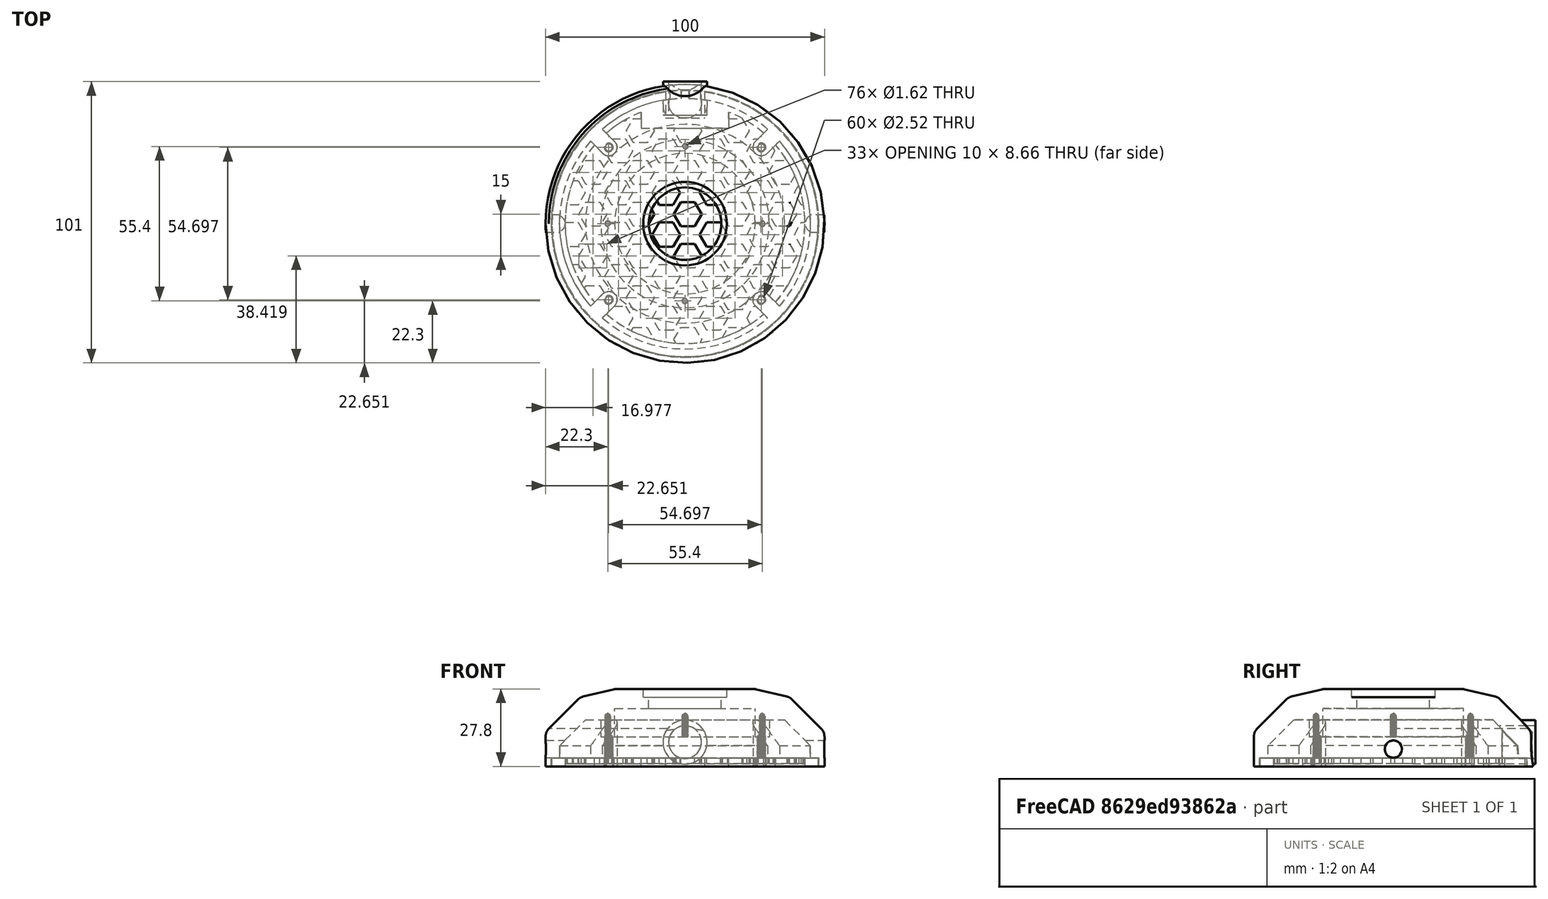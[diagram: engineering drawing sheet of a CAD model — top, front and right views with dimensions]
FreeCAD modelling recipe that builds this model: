
FCSTD DOCUMENT  (FreeCAD 0.22R37898 (Git))
Label: headset cup
License: All rights reserved
objects: Sketcher::SketchObject×12, PartDesign::Pad×4, PartDesign::Pocket×4, PartDesign::Body×3, PartDesign::PolarPattern×2, PartDesign::Hole×2, PartDesign::LinearPattern×2, PartDesign::Revolution×1, PartDesign::ShapeBinder×1, PartDesign::MultiTransform×1, PartDesign::Boolean×1, PartDesign::Fillet×1
note: 46 computed .brp shape members not serialized (recipe doc carries the construction recipe); baked Part::Feature solids carry a one-line shape summary decoded from their .brp

FEATURE [Sketcher::SketchObject] Sketch
  AttachmentSupport = -> [XZ_Plane]
  FullyConstrained = false
  MapMode = 5
  Placement = pos=(0,0,0) rot=(1,0,0;1.5708rad)
  sketch-geometry (23):
    g0: LineSegment StartX=-50 StartY=0 StartZ=0 EndX=-50 EndY=12.4 EndZ=0
    g1: LineSegment StartX=-50 StartY=12.4 StartZ=0 EndX=-37.6 EndY=12.4 EndZ=0
    g2: LineSegment StartX=-37.6 StartY=12.4 StartZ=0 EndX=-37.6 EndY=24.8 EndZ=0
    g3: LineSegment StartX=-50 StartY=12.4 StartZ=0 EndX=-37.6 EndY=24.8 EndZ=0
    g4: LineSegment StartX=-37.6 StartY=24.8 StartZ=0 EndX=0 EndY=24.8 EndZ=0
    g5: LineSegment StartX=-25 StartY=27.8 StartZ=0 EndX=-25 EndY=0.000476786 EndZ=0
    g6: LineSegment StartX=-37.6 StartY=24.8 StartZ=0 EndX=-25 EndY=27.8 EndZ=0
    g7: LineSegment StartX=-50 StartY=0 StartZ=0 EndX=-48 EndY=0 EndZ=0
    g8: LineSegment StartX=-48 StartY=0 StartZ=0 EndX=-48 EndY=3 EndZ=0
    g9: LineSegment StartX=-48 StartY=3 StartZ=0 EndX=-45 EndY=3 EndZ=0
    g10: LineSegment StartX=-45 StartY=7.4 StartZ=0 EndX=-45 EndY=3 EndZ=0
    g11: LineSegment StartX=-50 StartY=12.4 StartZ=0 EndX=-45 EndY=7.4 EndZ=0
    g12: LineSegment StartX=-45 StartY=7.4 StartZ=0 EndX=-35.6769 EndY=16.7231 EndZ=0
    g13: LineSegment StartX=-37.6 StartY=24.8 StartZ=0 EndX=-35.6769 EndY=16.7231 EndZ=0
    g14: LineSegment StartX=-30.2 StartY=10.6 StartZ=0 EndX=-25.2 EndY=10.6 EndZ=0
    g15: LineSegment StartX=-35.6769 StartY=16.7231 StartZ=0 EndX=-30.2 EndY=16.7231 EndZ=0
    g16: LineSegment StartX=-30.2 StartY=16.7231 StartZ=0 EndX=-30.2 EndY=10.6 EndZ=0
    g17: LineSegment StartX=-25.2 StartY=10.6 StartZ=0 EndX=-25.2 EndY=20.8 EndZ=0
    g18: LineSegment StartX=-25.2 StartY=20.8 StartZ=0 EndX=-13 EndY=20.8 EndZ=0
    g19: LineSegment StartX=-15 StartY=27.8 StartZ=0 EndX=-25 EndY=27.8 EndZ=0
    g20: LineSegment StartX=-13 StartY=20.8 StartZ=0 EndX=-13 EndY=24.8 EndZ=0
    g21: LineSegment StartX=-13 StartY=24.8 StartZ=0 EndX=-15 EndY=24.8 EndZ=0
    g22: LineSegment StartX=-15 StartY=24.8 StartZ=0 EndX=-15 EndY=27.8 EndZ=0
  constraints (63):
    c: PointOnObject(g0,g-1)
    c: Distance(g0) = 12.4
    c: Vertical(g0)
    c: Distance(g1) = 12.4
    c: Coincident(g1,g0)
    c: Horizontal(g1)
    c: Distance(g2) = 12.4
    c: Coincident(g2,g1)
    c: Vertical(g2)
    c: Coincident(g3,g0)
    c: Coincident(g3,g2)
    c: Coincident(g4,g2)
    c: PointOnObject(g4,g-2)
    c: Horizontal(g4)
    c: Vertical(g5)
    c: Distance(g-2,g5) = 25
    c: Coincident(g6,g2)
    c: Block(g6)
    c: Distance(g7) = 2
    c: Coincident(g7,g0)
    c: PointOnObject(g7,g-1)
    c: Distance(g8) = 3
    c: Coincident(g8,g7)
    c: Vertical(g8)
    c: Distance(g9) = 3
    c: Coincident(g9,g8)
    c: Horizontal(g9)
    c: Vertical(g10)
    c: Coincident(g10,g9)
    c: Coincident(g11,g0)
    c: Angle(g11,g3) = 1.5708
    c: Coincident(g11,g10)
    c: Coincident(g12,g10)
    c: Parallel(g12,g3)
    c: Coincident(g13,g2)
    c: Perpendicular(g6,g13)
    c: Coincident(g12,g13)
    c: Horizontal(g14)
    c: Coincident(g15,g12)
    c: Horizontal(g15)
    c: Distance(g15,g5) = 5.2
    c: Coincident(g16,g15)
    c: Vertical(g16)
    c: Coincident(g14,g16)
    c: Distance(g6,g14) = 17.2
    c: Coincident(g5,g6)
    c: Coincident(g17,g14)
    c: Vertical(g17)
    c: Distance(g17,g4) = 4
    c: Perpendicular(g18,g17) = 1.5708
    c: Coincident(g19,g5)
    c: Horizontal(g19)
    c: Distance(g5,g17) = 0.2
    c: Distance(g18,g18) = 12.2
    c: Coincident(g20,g18)
    c: PointOnObject(g20,g4)
    c: Vertical(g20)
    c: Coincident(g21,g20)
    c: PointOnObject(g21,g4)
    c: Coincident(g22,g21)
    c: Vertical(g22)
    c: Coincident(g22,g19)
    c: DistanceX(g21,g21) = 2
FEATURE [Sketcher::SketchObject] Sketch003
  FullyConstrained = false
  MapMode = 5
  Placement = pos=(0,7e-16,3) rot=(1,0,0;3.14159rad)
  sketch-geometry (4):
    g0: Circle CenterX=-0.037202 CenterY=-40.3385 CenterZ=0 NormalX=0 NormalY=0 NormalZ=1 AngleXU=0 Radius=1.53995
    g1: Circle CenterX=40.3385 CenterY=-0.037202 CenterZ=0 NormalX=0 NormalY=0 NormalZ=1 AngleXU=0 Radius=1.48786
    g2: Circle CenterX=0.037202 CenterY=40.3385 CenterZ=0 NormalX=0 NormalY=0 NormalZ=1 AngleXU=0 Radius=1.46013
    g3: Circle CenterX=-40.3385 CenterY=0.037202 CenterZ=0 NormalX=0 NormalY=0 NormalZ=1 AngleXU=0 Radius=1.54339
FEATURE [PartDesign::Revolution] Revolution
  Angle = 360
  Angle2 = 60
  Axis = (0,2e-16,1)
  Base = (0,0,0)
  Placement = pos=(0,0,0) rot=(1,0,0;1.5708rad)
  Profile = -> Sketch
  ReferenceAxis = -> Sketch [V_Axis]
  Refine = true
  Suppressed = false
  Type = 0
FEATURE [Sketcher::SketchObject] Sketch004  label="support for screws"
  AttachmentSupport = -> [Revolution]
  FullyConstrained = false
  MapMode = 5
  Placement = pos=(0,7e-16,3) rot=(1,0,0;3.14159rad)
  sketch-geometry (6):
    g0: LineSegment StartX=0 StartY=0 StartZ=0 EndX=54.6974 EndY=54.6974 EndZ=0
    g1: Circle CenterX=27.3487 CenterY=27.3487 CenterZ=0 NormalX=0 NormalY=0 NormalZ=1 AngleXU=0 Radius=1.5
    g2: ArcOfCircle CenterX=27.3487 CenterY=27.3487 CenterZ=0 NormalX=0 NormalY=0 NormalZ=1 AngleXU=0 Radius=3 StartAngle=2.3562 EndAngle=5.49778
    g3: ArcOfCircle CenterX=9.84391e-06 CenterY=0 CenterZ=0 NormalX=0 NormalY=0 NormalZ=1 AngleXU=0 Radius=45 StartAngle=0.718682 EndAngle=0.852114
    g4: LineSegment StartX=25.2274 StartY=29.47 StartZ=0 EndX=29.6277 EndY=33.8703 EndZ=0
    g5: LineSegment StartX=33.8703 StartY=29.6277 StartZ=0 EndX=29.47 EndY=25.2274 EndZ=0
  constraints (14):
    c: Coincident(g0,g-1)
    c: Diameter(g1) = 3
    c: Symmetric(g0,g0,g1)
    c: Tangent(g2,g1) = -1.5708
    c: Coincident(g4,g2)
    c: Coincident(g4,g3)
    c: Coincident(g5,g3)
    c: Coincident(g5,g2)
    c: Equal(g5,g4)
    c: Parallel(g5,g0)
    c: Parallel(g4,g0)
    c: Block(g3)
    c: Radius(g2) = 3
    c: Angle(g0,g-2) = 0.785398
FEATURE [PartDesign::Pad] Pad  label="support screws"
  BaseFeature = -> Revolution
  Direction = (0,0,-1)
  Length = 10
  Length2 = 10
  Placement = pos=(0,0,0) rot=(1,0,0;1.5708rad)
  Profile = -> Sketch004
  ReferenceAxis = -> Sketch004 [N_Axis]
  Refine = true
  Reversed = true
  Suppressed = false
  Type = 5
FEATURE [Sketcher::SketchObject] Sketch005
  FullyConstrained = false
  MapMode = 5
  Placement = pos=(0,7e-16,3) rot=(1,0,0;3.14159rad)
  sketch-geometry (4):
    g0: Circle CenterX=-27.3487 CenterY=27.3487 CenterZ=0 NormalX=0 NormalY=0 NormalZ=1 AngleXU=0 Radius=1.5
    g1: Circle CenterX=27.3487 CenterY=27.3487 CenterZ=0 NormalX=0 NormalY=0 NormalZ=1 AngleXU=0 Radius=1.5
    g2: Circle CenterX=27.3487 CenterY=-27.3487 CenterZ=0 NormalX=0 NormalY=0 NormalZ=1 AngleXU=0 Radius=1.5
    g3: Circle CenterX=-27.3487 CenterY=-27.3487 CenterZ=0 NormalX=0 NormalY=0 NormalZ=1 AngleXU=0 Radius=1.5
  constraints (4):
    c: Diameter(g0) = 3
    c: Diameter(g1) = 3
    c: Diameter(g2) = 3
    c: Diameter(g3) = 3
FEATURE [Sketcher::SketchObject] Sketch006
  FullyConstrained = false
  MapMode = 5
  Placement = pos=(58,0,0) rot=(0.57735,0.57735,0.57735;2.0944rad)
  sketch-geometry (3):
    g0: LineSegment StartX=2.9e-15 StartY=12.4 StartZ=0 EndX=0 EndY=0 EndZ=0
    g1: LineSegment StartX=-10.7592 StartY=6.2 StartZ=0 EndX=0 EndY=6.2 EndZ=0
    g2: Circle CenterX=0 CenterY=6.2 CenterZ=0 NormalX=0 NormalY=0 NormalZ=1 AngleXU=0 Radius=3.1
  constraints (5):
    c: Coincident(g0,g-1)
    c: Symmetric(g0,g0,g1)
    c: PointOnObject(g1,g0)
    c: Diameter(g2) = 6.2
    c: Coincident(g2,g1)
FEATURE [Sketcher::SketchObject] Sketch007
  FullyConstrained = false
  MapMode = 5
  Placement = pos=(0,2.4e-15,10.6) rot=(1,0,0;3.14159rad)
  sketch-geometry (5):
    g0: LineSegment StartX=-7.92396 StartY=-25.2 StartZ=0 EndX=7.02985 EndY=-25.2 EndZ=0
    g1: LineSegment StartX=-7.20371 StartY=-30.2 StartZ=0 EndX=7.21561 EndY=-30.2 EndZ=0
    g2: LineSegment StartX=0 StartY=-25.2 StartZ=0 EndX=0 EndY=-30.2 EndZ=0
    g3: LineSegment StartX=-3.01823 StartY=-27.7 StartZ=0 EndX=0 EndY=-27.7 EndZ=0
    g4: Circle CenterX=0 CenterY=-27.7 CenterZ=0 NormalX=0 NormalY=0 NormalZ=1 AngleXU=0 Radius=1
  constraints (9):
    c: Horizontal(g0)
    c: Horizontal(g1)
    c: PointOnObject(g2,g0)
    c: PointOnObject(g2,g1)
    c: Horizontal(g3)
    c: Symmetric(g2,g2,g3)
    c: PointOnObject(g3,g2)
    c: Diameter(g4) = 2
    c: Coincident(g4,g3)
FEATURE [Sketcher::SketchObject] Sketch008
  FullyConstrained = false
  MapMode = 5
  Placement = pos=(0,38,4) rot=(1,0,0;1.5708rad)
  sketch-geometry (3):
    g0: LineSegment StartX=-2.7e-15 StartY=9.4 StartZ=0 EndX=0 EndY=0 EndZ=0
    g1: LineSegment StartX=-8.38522 StartY=4.7 StartZ=0 EndX=-1.8e-15 EndY=4.7 EndZ=0
    g2: Circle CenterX=-1.8e-15 CenterY=4.7 CenterZ=0 NormalX=0 NormalY=0 NormalZ=1 AngleXU=0 Radius=5.85
  constraints (5):
    c: Coincident(g0,g-1)
    c: Symmetric(g0,g0,g1)
    c: PointOnObject(g1,g0)
    c: Diameter(g2) = 11.7
    c: Coincident(g2,g1)
FEATURE [Sketcher::SketchObject] Sketch009
  FullyConstrained = false
  MapMode = 5
  Placement = pos=(0,39,1) rot=(1,0,0;1.5708rad)
  sketch-geometry (4):
    g0: LineSegment StartX=0 StartY=13.6019 StartZ=0 EndX=0 EndY=1.80165 EndZ=0
    g1: LineSegment StartX=3.124 StartY=7.70178 StartZ=0 EndX=0 EndY=7.70178 EndZ=0
    g2: Circle CenterX=0 CenterY=7.70178 CenterZ=0 NormalX=0 NormalY=0 NormalZ=1 AngleXU=0 Radius=5.90013
    g3: Circle CenterX=0 CenterY=7.70178 CenterZ=0 NormalX=0 NormalY=0 NormalZ=1 AngleXU=0 Radius=7.90013
  constraints (8):
    c: PointOnObject(g0,g-2)
    c: Vertical(g0)
    c: Symmetric(g0,g0,g1)
    c: PointOnObject(g1,g0)
    c: Coincident(g2,g1)
    c: PointOnObject(g0,g2)
    c: Coincident(g3,g1)
    c: Distance(g3,g2) = 2
FEATURE [PartDesign::PolarPattern] PolarPattern
  Angle = 360
  Axis = -> Sketch004 [N_Axis]
  BaseFeature = -> Pad
  Mode = 0
  Occurrences = 4
  Offset = 120
  Originals = -> [Pad]
  Placement = pos=(0,0,0) rot=(1,0,0;1.5708rad)
  Refine = true
  Suppressed = false
  TransformMode = 0
FEATURE [PartDesign::Hole] Hole
  BaseFeature = -> PolarPattern
  CustomThreadClearance = 0
  Depth = 8
  DepthType = 0
  Diameter = 2.52
  DrillForDepth = false
  DrillPoint = 1
  DrillPointAngle = 118
  HoleCutCountersinkAngle = 90
  HoleCutCustomValues = false
  HoleCutDepth = 0
  HoleCutDiameter = 6.1
  HoleCutType = 0
  ModelThread = true
  Placement = pos=(0,0,0) rot=(1,0,0;1.5708rad)
  Profile = -> Sketch005
  Refine = true
  Suppressed = false
  Tapered = false
  TaperedAngle = 90
  ThreadClass = 0
  ThreadDepth = 8
  ThreadDepthType = 0
  ThreadDirection = 0
  ThreadFit = 0
  ThreadSize = 9
  ThreadType = 1
  Threaded = true
  UseCustomThreadClearance = false
FEATURE [PartDesign::Pocket] Pocket
  BaseFeature = -> Hole
  Direction = (-1,1e-16,-2e-16)
  Length = 5
  Length2 = 5
  Placement = pos=(0,0,0) rot=(1,0,0;1.5708rad)
  Profile = -> Sketch006
  ReferenceAxis = -> Sketch006 [N_Axis]
  Refine = true
  Suppressed = false
  Type = 1
FEATURE [PartDesign::Hole] Hole001  label="driver holes"
  BaseFeature = -> Pocket
  CustomThreadClearance = 0
  Depth = 8
  DepthType = 0
  Diameter = 1.619
  DrillForDepth = false
  DrillPoint = 1
  DrillPointAngle = 118
  HoleCutCountersinkAngle = 90
  HoleCutCustomValues = false
  HoleCutDepth = 0
  HoleCutDiameter = 6.1
  HoleCutType = 0
  ModelThread = true
  Placement = pos=(0,0,0) rot=(1,0,0;1.5708rad)
  Profile = -> Sketch007
  Refine = true
  Suppressed = false
  Tapered = false
  TaperedAngle = 90
  ThreadClass = 0
  ThreadDepth = 8
  ThreadDepthType = 0
  ThreadDirection = 0
  ThreadFit = 0
  ThreadSize = 6
  ThreadType = 1
  Threaded = true
  UseCustomThreadClearance = false
FEATURE [PartDesign::PolarPattern] PolarPattern001
  Angle = 360
  Axis = -> Sketch007 [N_Axis]
  BaseFeature = -> Hole001
  Mode = 0
  Occurrences = 4
  Offset = 120
  Originals = -> [Hole001]
  Placement = pos=(0,0,0) rot=(1,0,0;1.5708rad)
  Refine = true
  Suppressed = false
  TransformMode = 0
FEATURE [PartDesign::Pocket] Pocket001  label="hirose holes"
  BaseFeature = -> PolarPattern001
  Direction = (0,1,0)
  Length = 5
  Length2 = 5
  Placement = pos=(0,0,0) rot=(1,0,0;1.5708rad)
  Profile = -> Sketch008
  ReferenceAxis = -> Sketch008 [N_Axis]
  Refine = true
  Suppressed = false
  Type = 1
FEATURE [PartDesign::Pad] Pad001
  BaseFeature = -> Pocket001
  Direction = (0,-1,0)
  Length = 12
  Length2 = 10
  Placement = pos=(0,0,0) rot=(1,0,0;1.5708rad)
  Profile = -> Sketch009
  ReferenceAxis = -> Sketch009 [N_Axis]
  Refine = true
  Reversed = true
  Suppressed = false
  Type = 0
FEATURE [PartDesign::ShapeBinder] CopyFillet
  Placement = pos=(0,0,0) rot=(1,0,0;1.5708rad)
  TraceSupport = false
FEATURE [Sketcher::SketchObject] Sketch010
  AttachmentSupport = -> [CopyFillet]
  ExternalGeometry = -> [CopyFillet]
  FullyConstrained = true
  MapMode = 5
  Placement = pos=(0,2e-15,3) rot=(1,0,0;3.14159rad)
  sketch-geometry (1):
    g0: Circle CenterX=0 CenterY=0 CenterZ=0 NormalX=0 NormalY=0 NormalZ=1 AngleXU=0 Radius=47.75
  constraints (2):
    c: Coincident(g0,g-1)
    c: Diameter(g0) = 95.5
FEATURE [PartDesign::Pad] Pad002
  Direction = (0,0,-1)
  Length = 2
  Length2 = 10
  Placement = pos=(0,0,0) rot=(1,0,0;1.5708rad)
  Profile = -> Sketch010
  ReferenceAxis = -> Sketch010 [N_Axis]
  Refine = true
  Suppressed = false
  Type = 0
FEATURE [Sketcher::SketchObject] Sketch011
  AttachmentSupport = -> [XY_Plane001]
  FullyConstrained = false
  MapMode = 5
  sketch-geometry (17):
    g0: LineSegment StartX=-45.0225 StartY=-41.5809 StartZ=0 EndX=-47.5225 EndY=-37.2507 EndZ=0
    g1: LineSegment StartX=-47.5225 StartY=-37.2507 StartZ=0 EndX=-52.5225 EndY=-37.2507 EndZ=0
    g2: LineSegment StartX=-52.5225 StartY=-37.2507 StartZ=0 EndX=-55.0225 EndY=-41.5809 EndZ=0
    g3: LineSegment StartX=-55.0225 StartY=-41.5809 StartZ=0 EndX=-52.5225 EndY=-45.911 EndZ=0
    g4: LineSegment StartX=-52.5225 StartY=-45.911 StartZ=0 EndX=-47.5225 EndY=-45.911 EndZ=0
    g5: LineSegment StartX=-47.5225 StartY=-45.911 StartZ=0 EndX=-45.0225 EndY=-41.5809 EndZ=0
    g6: Circle CenterX=-50.0225 CenterY=-41.5809 CenterZ=0 NormalX=0 NormalY=0 NormalZ=1 AngleXU=0 Radius=5
    g7: LineSegment StartX=-35.7904 StartY=-48.911 StartZ=0 EndX=-38.2904 EndY=-44.5809 EndZ=0
    g8: LineSegment StartX=-38.2904 StartY=-44.5809 StartZ=0 EndX=-43.2904 EndY=-44.5809 EndZ=0
    g9: LineSegment StartX=-43.2904 StartY=-44.5809 StartZ=0 EndX=-45.7904 EndY=-48.911 EndZ=0
    g10: LineSegment StartX=-45.7904 StartY=-48.911 StartZ=0 EndX=-43.2904 EndY=-53.2411 EndZ=0
    g11: LineSegment StartX=-43.2904 StartY=-53.2411 StartZ=0 EndX=-38.2904 EndY=-53.2411 EndZ=0
    g12: LineSegment StartX=-38.2904 StartY=-53.2411 StartZ=0 EndX=-35.7904 EndY=-48.911 EndZ=0
    g13: Circle CenterX=-40.7904 CenterY=-48.911 CenterZ=0 NormalX=0 NormalY=0 NormalZ=1 AngleXU=0 Radius=5
    g14: LineSegment StartX=-45.0225 StartY=-41.5809 StartZ=0 EndX=-43.2904 EndY=-44.5809 EndZ=0
    g15: LineSegment StartX=-43.2904 StartY=-44.5809 StartZ=0 EndX=-41.5584 EndY=-41.5809 EndZ=0
    g16: LineSegment StartX=-41.5584 StartY=-41.5809 StartZ=0 EndX=-45.0225 EndY=-41.5809 EndZ=0
  constraints (39):
    c: Coincident(g0,g1)
    c: Coincident(g1,g2)
    c: Coincident(g2,g3)
    c: Coincident(g3,g4)
    c: Coincident(g4,g5)
    c: Coincident(g5,g0)
    c: Equal(g0, g1-g5) x5
    c: PointOnObject(g0,g6)
    c: PointOnObject(g1,g6)
    c: PointOnObject(g2,g6)
    c: PointOnObject(g3,g6)
    c: PointOnObject(g4,g6)
    c: PointOnObject(g5,g6)
    c: Radius(g6) = 5
    c: Coincident(g7,g8)
    c: Coincident(g8,g9)
    c: Coincident(g9,g10)
    c: Coincident(g10,g11)
    c: Coincident(g11,g12)
    c: Coincident(g12,g7)
    c: Equal(g7, g8-g12) x5
    c: PointOnObject(g7,g13)
    c: PointOnObject(g8,g13)
    c: PointOnObject(g9,g13)
    c: PointOnObject(g10,g13)
    c: PointOnObject(g11,g13)
    c: PointOnObject(g12,g13)
    c: Radius(g13) = 5
    c: Coincident(g14,g0)
    c: Coincident(g14,g8)
    c: Coincident(g15,g8)
    c: Coincident(g16,g15)
    c: Coincident(g16,g0)
    c: Equal(g16,g15)
    c: Equal(g15,g14)
    c: Horizontal(g16)
    c: Horizontal(g8)
    c: Horizontal(g1)
    c: DistanceY(g15,g15) = 3
FEATURE [PartDesign::Pocket] Pocket002
  BaseFeature = -> Pad002
  Direction = (0,0,-1)
  Length = 5
  Length2 = 5
  Placement = pos=(0,0,0) rot=(1,0,0;1.5708rad)
  Profile = -> Sketch011
  ReferenceAxis = -> Sketch011 [N_Axis]
  Refine = true
  Reversed = true
  Suppressed = false
  Type = 0
FEATURE [PartDesign::LinearPattern] LinearPattern
  Direction = -> Sketch011 [H_Axis]
  Length = 85
  Mode = 1
  Occurrences = 6
  Offset = 17
  Placement = pos=(0,0,0) rot=(1,0,0;1.5708rad)
  Refine = true
  Suppressed = false
  TransformMode = 0
FEATURE [PartDesign::LinearPattern] LinearPattern001
  Direction = -> Sketch011 [V_Axis]
  Length = 90
  Mode = 1
  Occurrences = 7
  Offset = 15
  Placement = pos=(0,0,0) rot=(1,0,0;1.5708rad)
  Refine = true
  Suppressed = false
  TransformMode = 0
FEATURE [PartDesign::MultiTransform] MultiTransform
  BaseFeature = -> Pocket002
  Originals = -> [Pocket002]
  Placement = pos=(0,0,0) rot=(1,0,0;1.5708rad)
  Refine = true
  Suppressed = false
  TransformMode = 0
  Transformations = -> [LinearPattern,LinearPattern001]
FEATURE [Sketcher::SketchObject] Sketch012
  AttachmentSupport = -> [XY_Plane002]
  ExternalGeometry = -> [MultiTransform]
  FullyConstrained = false
  MapMode = 5
  sketch-geometry (29):
    g0: Circle CenterX=0 CenterY=0 CenterZ=0 NormalX=0 NormalY=0 NormalZ=1 AngleXU=0 Radius=47.75
    g1: LineSegment StartX=-57.5555 StartY=57.5555 StartZ=0 EndX=50.8386 EndY=-50.8386 EndZ=0
    g2: ArcOfCircle CenterX=0 CenterY=0 CenterZ=0 NormalX=0 NormalY=0 NormalZ=1 AngleXU=0 Radius=38.695 StartAngle=3.92699 EndAngle=5.49779
    g3: LineSegment StartX=-51.8471 StartY=-51.8471 StartZ=0 EndX=73.892 EndY=73.892 EndZ=0
    g4: ArcOfCircle CenterX=0 CenterY=0 CenterZ=0 NormalX=0 NormalY=0 NormalZ=1 AngleXU=0 Radius=38.695 StartAngle=0.785398 EndAngle=2.35619
    g5: Circle CenterX=-27.3615 CenterY=27.3615 CenterZ=0 NormalX=0 NormalY=0 NormalZ=1 AngleXU=0 Radius=1.5
    g6: Circle CenterX=27.3615 CenterY=27.3615 CenterZ=0 NormalX=0 NormalY=0 NormalZ=1 AngleXU=0 Radius=1.5
    g7: Circle CenterX=27.3615 CenterY=-27.3615 CenterZ=0 NormalX=0 NormalY=0 NormalZ=1 AngleXU=0 Radius=1.5
    g8: Circle CenterX=-27.3615 CenterY=-27.3615 CenterZ=0 NormalX=0 NormalY=0 NormalZ=1 AngleXU=0 Radius=1.5
    g9: ArcOfCircle CenterX=0 CenterY=0 CenterZ=0 NormalX=0 NormalY=0 NormalZ=1 AngleXU=0 Radius=43.0003 StartAngle=5.56761 EndAngle=6.99876
    g10: ArcOfCircle CenterX=27.3615 CenterY=-27.3615 CenterZ=0 NormalX=0 NormalY=0 NormalZ=1 AngleXU=0 Radius=3 StartAngle=0.785398 EndAngle=3.88822
    g11: LineSegment StartX=25.1595 StartY=-29.399 StartZ=0 EndX=28.2121 EndY=-32.4516 EndZ=0
    g12: LineSegment StartX=29.4828 StartY=-25.2402 StartZ=0 EndX=32.4531 EndY=-28.2104 EndZ=0
    g13: ArcOfCircle CenterX=-27.3983 CenterY=-27.3613 CenterZ=0 NormalX=0 NormalY=0 NormalZ=1 AngleXU=0 Radius=3 StartAngle=5.50055 EndAngle=8.63075
    g14: LineSegment StartX=-25.2711 StartY=-29.4768 StartZ=0 EndX=-28.2302 EndY=-32.4359 EndZ=0
    g15: LineSegment StartX=-29.5012 StartY=-25.2218 StartZ=0 EndX=-32.4702 EndY=-28.1907 EndZ=0
    g16: ArcOfCircle CenterX=0 CenterY=0 CenterZ=0 NormalX=0 NormalY=0 NormalZ=1 AngleXU=0 Radius=43.0003 StartAngle=3.99621 EndAngle=5.42802
    g17: ArcOfCircle CenterX=-27.3983 CenterY=27.3613 CenterZ=0 NormalX=0 NormalY=0 NormalZ=1 AngleXU=0 Radius=3 StartAngle=3.93563 EndAngle=7.06582
    g18: ArcOfCircle CenterX=27.3615 CenterY=27.3615 CenterZ=0 NormalX=0 NormalY=0 NormalZ=1 AngleXU=0 Radius=3 StartAngle=2.35619 EndAngle=5.49779
    g19: ArcOfCircle CenterX=0 CenterY=0 CenterZ=0 NormalX=0 NormalY=0 NormalZ=1 AngleXU=0 Radius=43.0003 StartAngle=2.42662 EndAngle=3.85656
    g20: ArcOfCircle CenterX=0 CenterY=0 CenterZ=0 NormalX=0 NormalY=0 NormalZ=1 AngleXU=0 Radius=43.0003 StartAngle=0.855222 EndAngle=1.19704
    g21: LineSegment StartX=25.2402 StartY=29.4828 StartZ=0 EndX=28.2104 EndY=32.4531 EndZ=0
    g22: LineSegment StartX=-15.7 StartY=40.0317 StartZ=0 EndX=-15.7 EndY=34.3 EndZ=0
    g23: LineSegment StartX=15.7 StartY=40.0317 StartZ=0 EndX=15.7 EndY=34.3 EndZ=0
    g24: LineSegment StartX=-15.7 StartY=34.3 StartZ=0 EndX=15.7 EndY=34.3 EndZ=0
    g25: ArcOfCircle CenterX=0 CenterY=0 CenterZ=0 NormalX=0 NormalY=0 NormalZ=1 AngleXU=0 Radius=43.0003 StartAngle=1.94455 EndAngle=2.28698
    g26: LineSegment StartX=29.4828 StartY=25.2402 StartZ=0 EndX=32.4531 EndY=28.2104 EndZ=0
    g27: LineSegment StartX=-25.2711 StartY=29.4768 StartZ=0 EndX=-28.2302 EndY=32.4359 EndZ=0
    g28: LineSegment StartX=-29.5012 StartY=25.2218 StartZ=0 EndX=-32.4702 EndY=28.1907 EndZ=0
  constraints (68):
    c: Coincident(g0,g-1)
    c: PointOnObject(g0,g1)
    c: Angle(g1,g-1) = 0.785398
    c: Coincident(g2,g0)
    c: Diameter(g2) = 77.39
    c: Perpendicular(g1,g3)
    c: PointOnObject(g0,g3)
    c: PointOnObject(g4,g1)
    c: PointOnObject(g2,g3)
    c: Equal(g2,g4)
    c: PointOnObject(g2,g1)
    c: PointOnObject(g4,g3)
    c: Coincident(g2,g4)
    c: Diameter(g5) = 3
    c: Coincident(g5,g4)
    c: Diameter(g6) = 3
    c: Coincident(g6,g4)
    c: Diameter(g7) = 3
    c: Coincident(g7,g2)
    c: Diameter(g8) = 3
    c: Coincident(g8,g2)
    c: Coincident(g9,g0)
    c: Diameter(g10) = 6
    c: Coincident(g10,g2)
    c: Parallel(g12,g1)
    c: Parallel(g1,g11)
    c: PointOnObject(g11,g2)
    c: Tangent(g10,g12) = 1.5708
    c: Coincident(g16,g11)
    c: Coincident(g9,g12)
    c: Diameter(g13) = 6
    c: Coincident(g14,g13)
    c: PointOnObject(g14,g9)
    c: Parallel(g14,g3)
    c: Coincident(g15,g13)
    c: Parallel(g15,g3)
    c: Equal(g9,g16)
    c: Coincident(g19,g15)
    c: Coincident(g9,g16)
    c: PointOnObject(g16,g14)
    c: Diameter(g18) = 6
    c: Diameter(g17) = 6
    c: Equal(g9,g19)
    c: Coincident(g9,g19)
    c: Equal(g9,g20)
    c: Coincident(g9,g20)
    c: Coincident(g21,g18)
    c: Coincident(g21,g20)
    c: Parallel(g21,g3)
    c: Coincident(g11,g10)
    c: Vertical(g22)
    c: Vertical(g23)
    c: Coincident(g24,g22)
    c: Horizontal(g24)
    c: Coincident(g23,g24)
    c: Equal(g20,g25)
    c: Coincident(g20,g23)
    c: Coincident(g25,g22)
    c: Coincident(g20,g25)
    c: Distance(g22,g-2) = 15.7
    c: Distance(g23,g-2) = 15.7
    c: Coincident(g26,g18)
    c: Coincident(g26,g9)
    c: Coincident(g27,g17)
    c: Coincident(g27,g25)
    c: Coincident(g28,g17)
    c: Coincident(g28,g19)
    c: Diameter(g0) = 95.5
FEATURE [PartDesign::Pad] Pad003
  Direction = (0,0,1)
  Length = 3
  Length2 = 10
  Profile = -> Sketch012
  ReferenceAxis = -> Sketch012 [N_Axis]
  Refine = true
  Suppressed = false
  Type = 0
FEATURE [PartDesign::Body] Body002  label="rejilla2"
  AllowCompound = false
  Group = -> [Sketch012,Pad003]
  Origin = -> Origin002
  Tip = -> Pad003
FEATURE [Sketcher::SketchObject] Sketch013
  FullyConstrained = false
  Placement = pos=(0,0,3) rot=(0,0,1;0rad)
  sketch-geometry (8):
    g0: Circle CenterX=27.3615 CenterY=27.3615 CenterZ=0 NormalX=0 NormalY=0 NormalZ=1 AngleXU=0 Radius=1.59855
    g1: Circle CenterX=27.3615 CenterY=-27.3615 CenterZ=0 NormalX=0 NormalY=0 NormalZ=1 AngleXU=0 Radius=1.59855
    g2: Circle CenterX=-27.3615 CenterY=27.3615 CenterZ=0 NormalX=0 NormalY=0 NormalZ=1 AngleXU=0 Radius=1.59855
    g3: Circle CenterX=-27.3615 CenterY=-27.3615 CenterZ=0 NormalX=0 NormalY=0 NormalZ=1 AngleXU=0 Radius=1.59855
    g4: LineSegment StartX=-7 StartY=48 StartZ=0 EndX=7 EndY=48 EndZ=0
    g5: LineSegment StartX=-7 StartY=48 StartZ=0 EndX=-7 EndY=38 EndZ=0
    g6: LineSegment StartX=7 StartY=48 StartZ=0 EndX=7 EndY=38 EndZ=0
    g7: LineSegment StartX=-7 StartY=38 StartZ=0 EndX=7 EndY=38 EndZ=0
  constraints (10):
    c: Horizontal(g4)
    c: Coincident(g5,g4)
    c: Vertical(g5)
    c: Coincident(g6,g4)
    c: Vertical(g6)
    c: Block(g4)
    c: DistanceY(g6,g6) = 10
    c: Equal(g5,g6)
    c: Coincident(g7,g5)
    c: Coincident(g7,g6)
FEATURE [PartDesign::Boolean] Boolean
  BaseFeature = -> MultiTransform
  Group = -> [Body002]
  Refine = true
  Suppressed = false
  Type = 0
  UsePlacement = true
FEATURE [PartDesign::Pocket] Pocket003
  BaseFeature = -> Boolean
  Direction = (0,0,-1)
  Length = 5
  Length2 = 5
  Profile = -> Sketch013
  ReferenceAxis = -> Sketch013 [N_Axis]
  Refine = true
  Suppressed = false
  Type = 0
FEATURE [PartDesign::Body] Body001  label="grid"
  AllowCompound = false
  Group = -> [CopyFillet,Sketch010,Pad002,Sketch011,Pocket002,MultiTransform,LinearPattern,LinearPattern001,Boolean,Sketch013,Pocket003]
  Origin = -> Origin001
  Tip = -> Pocket003
FEATURE [PartDesign::Fillet] Fillet
  Base = -> Pad001 [Edge178,Edge181,Edge300,Edge385]
  BaseFeature = -> Pad001
  Placement = pos=(0,0,0) rot=(1,0,0;1.5708rad)
  Radius = 4
  Refine = true
  SupportTransform = false
  Suppressed = false
  UseAllEdges = false
FEATURE [PartDesign::Body] Body  label="cup"
  AllowCompound = false
  Group = -> [Sketch,Sketch003,Revolution,Sketch004,Pad,Sketch005,Sketch006,Sketch007,Sketch008,Sketch009,PolarPattern,Hole,Pocket,Hole001,PolarPattern001,Pocket001,Pad001,Fillet]
  Origin = -> Origin
  Tip = -> Fillet
